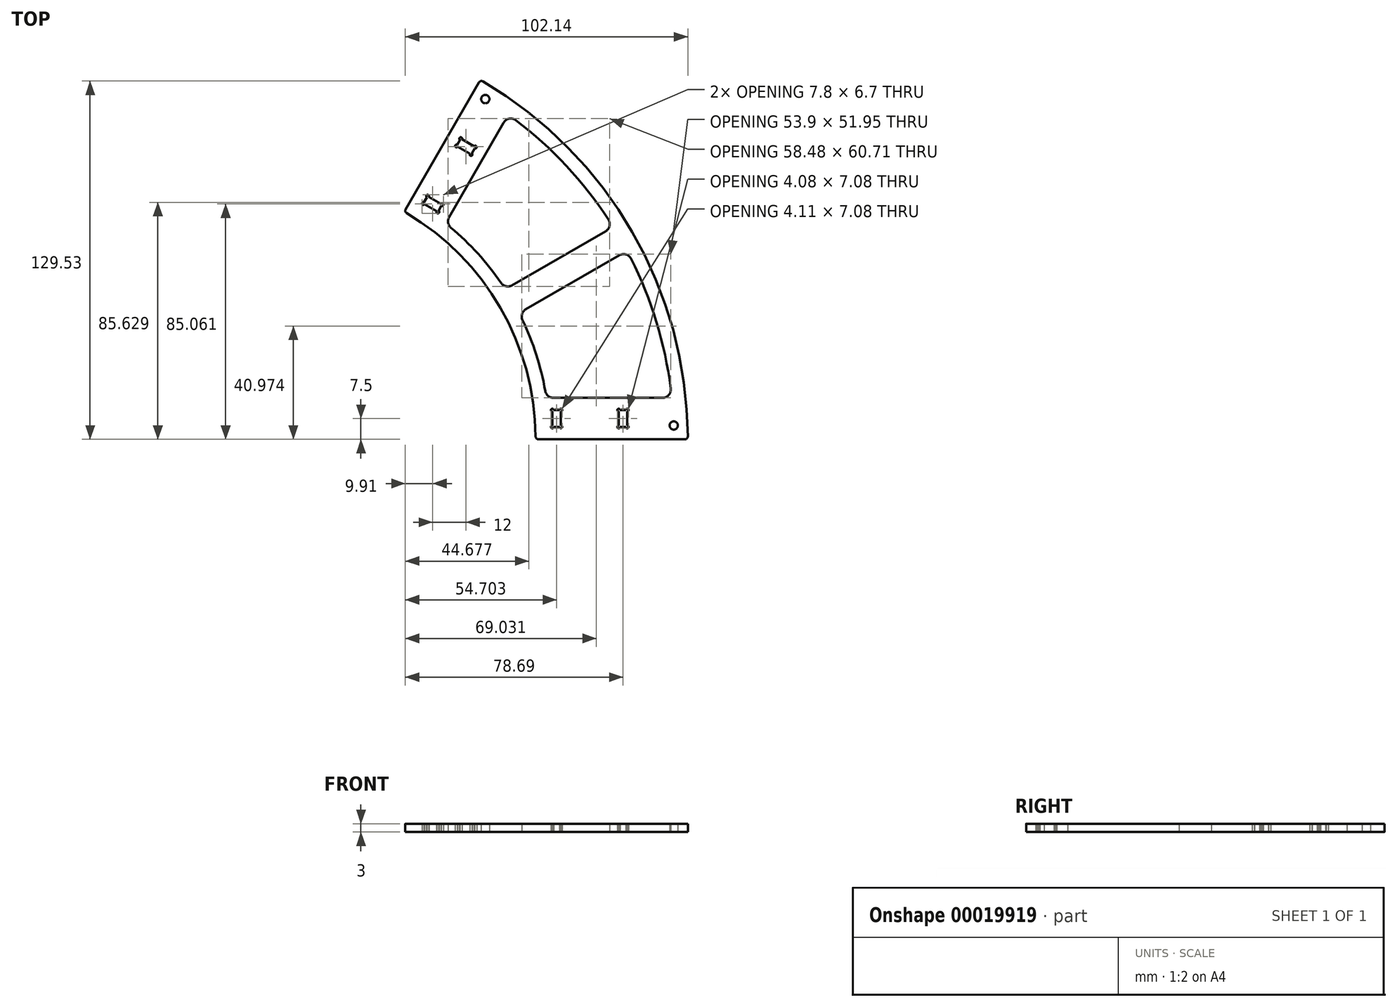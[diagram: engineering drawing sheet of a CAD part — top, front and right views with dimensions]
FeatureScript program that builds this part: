
annotation { "Feature Type Name" : "Feature", "Feature Type Description" : "" }
export const myFeature = defineFeature(function(context is Context, id is Id, definition is map)
    precondition{}
    {
        {
            var Q0;
            Q0=qCreatedBy(makeId("Top.planeOp"),FACE);
            var sketch = newSketch(context, id + "F1", { "sketchPlane" : qUnion([Q0])});
            skArc(sketch, "E0", {"start": v(150, 1) * mm, "mid": v(129.9, 75) * mm, "end": v(75.87, 129.4) * mm});
            skArc(sketch, "E1", {"start": v(95, 0.99) * mm, "mid": v(82.27, 47.5) * mm, "end": v(48.35, 81.77) * mm});
            skLineSegment(sketch, "E2", {"start": v(95, 0) * mm, "end": v(150, 0) * mm});
            skLineSegment(sketch, "E3", {"start": v(149, 0) * mm, "end": v(96, 0) * mm});
            skLineSegment(sketch, "E4", {"start": v(74.5, 129.03) * mm, "end": v(48, 83.13) * mm});
            skArc(sketch, "E5", {"start": v(143.83, 18.38) * mm, "mid": v(138.64, 42.46) * mm, "end": v(129.46, 65.31) * mm});
            skArc(sketch, "E6", {"start": v(98.46, 17.48) * mm, "mid": v(95.21, 30.58) * mm, "end": v(90.22, 43.12) * mm});
            skLineSegment(sketch, "E7", {"start": v(63.7, 80.33) * mm, "end": v(83.42, 114.48) * mm});
            skLineSegment(sketch, "E8", {"start": v(101.41, 15) * mm, "end": v(140.85, 15) * mm});
            skLineSegment(sketch, "E9", {"start": v(86.43, 55.67) * mm, "end": v(120.28, 75.22) * mm});
            skLineSegment(sketch, "E10", {"start": v(91.43, 47.01) * mm, "end": v(125.28, 66.56) * mm});
            skArc(sketch, "E11.trimOffspring", {"start": v(82.46, 56.58) * mm, "mid": v(74.09, 67.17) * mm, "end": v(64.37, 76.53) * mm});
            skArc(sketch, "E12.trimOffspring", {"start": v(121.29, 79.46) * mm, "mid": v(106.1, 98.84) * mm, "end": v(87.83, 115.37) * mm});
            skLineSegment(sketch, "E13", {"start": v(0, 0) * mm, "end": v(189.98, 109.68) * mm, "construction": true});
            skPoint(sketch, "E14.visualSharp", {"position": v(85.1, 117.4) * mm});
            skArc(sketch, "E14.filletArc", {"start": v(87.83, 115.37) * mm, "mid": v(85.42, 115.92) * mm, "end": v(83.42, 114.48) * mm});
            skPoint(sketch, "E15.visualSharp", {"position": v(123, 76.79) * mm});
            skArc(sketch, "E15.filletArc", {"start": v(120.28, 75.22) * mm, "mid": v(121.7, 77.12) * mm, "end": v(121.29, 79.46) * mm});
            skPoint(sketch, "E16.visualSharp", {"position": v(128, 68.13) * mm});
            skArc(sketch, "E16.filletArc", {"start": v(129.46, 65.31) * mm, "mid": v(127.64, 66.83) * mm, "end": v(125.28, 66.56) * mm});
            skPoint(sketch, "E17.visualSharp", {"position": v(144.22, 15) * mm});
            skArc(sketch, "E17.filletArc", {"start": v(140.85, 15) * mm, "mid": v(143.1, 16.02) * mm, "end": v(143.83, 18.38) * mm});
            skPoint(sketch, "E18.visualSharp", {"position": v(98.87, 15) * mm});
            skArc(sketch, "E18.filletArc", {"start": v(98.46, 17.48) * mm, "mid": v(99.49, 15.7) * mm, "end": v(101.41, 15) * mm});
            skPoint(sketch, "E19.visualSharp", {"position": v(89, 45.6) * mm});
            skArc(sketch, "E19.filletArc", {"start": v(91.43, 47.01) * mm, "mid": v(90.07, 45.3) * mm, "end": v(90.22, 43.12) * mm});
            skPoint(sketch, "E20.visualSharp", {"position": v(84, 54.27) * mm});
            skArc(sketch, "E20.filletArc", {"start": v(82.46, 56.58) * mm, "mid": v(84.27, 55.35) * mm, "end": v(86.43, 55.67) * mm});
            skPoint(sketch, "E21.visualSharp", {"position": v(62.42, 78.12) * mm});
            skArc(sketch, "E21.filletArc", {"start": v(63.7, 80.33) * mm, "mid": v(63.34, 78.3) * mm, "end": v(64.37, 76.53) * mm});
            skPoint(sketch, "E22.visualSharp", {"position": v(47.5, 82.27) * mm});
            skArc(sketch, "E22.filletArc", {"start": v(48, 83.13) * mm, "mid": v(47.9, 82.38) * mm, "end": v(48.35, 81.77) * mm});
            skPoint(sketch, "E23.visualSharp", {"position": v(75, 129.9) * mm});
            skArc(sketch, "E23.filletArc", {"start": v(75.87, 129.4) * mm, "mid": v(75.1, 129.5) * mm, "end": v(74.5, 129.03) * mm});
            skPoint(sketch, "E24.visualSharp", {"position": v(150, 0) * mm});
            skArc(sketch, "E24.filletArc", {"start": v(149, 0) * mm, "mid": v(149.7, 0.3) * mm, "end": v(150, 1) * mm});
            skPoint(sketch, "E25.visualSharp", {"position": v(95, 0) * mm});
            skArc(sketch, "E25.filletArc", {"start": v(95, 0.99) * mm, "mid": v(95.3, 0.29) * mm, "end": v(96, 0) * mm});
            skLineSegment(sketch, "E26", {"start": v(100, 4.62) * mm, "end": v(100, -10.43) * mm, "construction": true});
            skLineSegment(sketch, "E27.bottom", {"start": v(101.5, 10.55) * mm, "end": v(103.6, 10.55) * mm});
            skLineSegment(sketch, "E27.top", {"start": v(101.5, 4.45) * mm, "end": v(103.62, 4.45) * mm});
            skLineSegment(sketch, "E27.left", {"start": v(101, 10.05) * mm, "end": v(101, 4.95) * mm});
            skLineSegment(sketch, "E27.right", {"start": v(104.1, 10.05) * mm, "end": v(104.1, 5) * mm});
            skArc(sketch, "E28", {"start": v(101.5, 10.55) * mm, "mid": v(100.65, 10.9) * mm, "end": v(101, 10.05) * mm});
            skArc(sketch, "E29", {"start": v(103.62, 4.45) * mm, "mid": v(104.5, 4.18) * mm, "end": v(104.1, 5) * mm});
            skArc(sketch, "E30", {"start": v(101, 4.95) * mm, "mid": v(100.65, 4.1) * mm, "end": v(101.5, 4.45) * mm});
            skArc(sketch, "E31", {"start": v(104.1, 10.05) * mm, "mid": v(104.45, 10.9) * mm, "end": v(103.6, 10.55) * mm});
            skLineSegment(sketch, "E32", {"start": v(36.09, 94.63) * mm, "end": v(64.73, 78.1) * mm, "construction": true});
            skLineSegment(sketch, "E33", {"start": v(54.79, 85) * mm, "end": v(59.2, 82.44) * mm});
            skLineSegment(sketch, "E34", {"start": v(59.89, 82.63) * mm, "end": v(60.94, 84.45) * mm});
            skLineSegment(sketch, "E35", {"start": v(60.75, 85.13) * mm, "end": v(56.34, 87.68) * mm});
            skLineSegment(sketch, "E36", {"start": v(54.6, 85.68) * mm, "end": v(55.65, 87.5) * mm});
            skArc(sketch, "E37", {"start": v(56.34, 87.68) * mm, "mid": v(55.77, 88.41) * mm, "end": v(55.65, 87.5) * mm});
            skArc(sketch, "E38", {"start": v(60.94, 84.45) * mm, "mid": v(61.67, 85) * mm, "end": v(60.75, 85.13) * mm});
            skArc(sketch, "E39", {"start": v(54.6, 85.68) * mm, "mid": v(53.87, 85.11) * mm, "end": v(54.79, 85) * mm});
            skArc(sketch, "E40", {"start": v(59.2, 82.44) * mm, "mid": v(59.77, 81.71) * mm, "end": v(59.89, 82.63) * mm});
            skCircle(sketch, "E41", {"center": v(144.91, 5) * mm, "radius": 1.5 * mm});
            skCircle(sketch, "E42", {"center": v(76.79, 123) * mm, "radius": 1.5 * mm});
            skLineSegment(sketch, "E43.bottom", {"start": v(125.5, 10.55) * mm, "end": v(127.6, 10.55) * mm});
            skLineSegment(sketch, "E43.top", {"start": v(125.5, 4.45) * mm, "end": v(127.6, 4.45) * mm});
            skLineSegment(sketch, "E43.left", {"start": v(125, 10.05) * mm, "end": v(125, 4.95) * mm});
            skLineSegment(sketch, "E43.right", {"start": v(128.1, 10.05) * mm, "end": v(128.1, 4.95) * mm});
            skArc(sketch, "E44", {"start": v(125.5, 10.55) * mm, "mid": v(124.65, 10.9) * mm, "end": v(125, 10.05) * mm});
            skArc(sketch, "E45", {"start": v(128.1, 10.05) * mm, "mid": v(128.45, 10.9) * mm, "end": v(127.6, 10.55) * mm});
            skArc(sketch, "E46", {"start": v(127.6, 4.45) * mm, "mid": v(128.45, 4.1) * mm, "end": v(128.1, 4.95) * mm});
            skArc(sketch, "E47", {"start": v(125, 4.95) * mm, "mid": v(124.65, 4.1) * mm, "end": v(125.5, 4.45) * mm});
            skLineSegment(sketch, "E48", {"start": v(66.79, 105.78) * mm, "end": v(71.2, 103.23) * mm});
            skLineSegment(sketch, "E49", {"start": v(71.89, 103.41) * mm, "end": v(72.94, 105.23) * mm});
            skLineSegment(sketch, "E50", {"start": v(72.75, 105.91) * mm, "end": v(68.34, 108.46) * mm});
            skLineSegment(sketch, "E51", {"start": v(67.65, 108.28) * mm, "end": v(66.6, 106.46) * mm});
            skArc(sketch, "E52", {"start": v(68.34, 108.46) * mm, "mid": v(67.77, 109.2) * mm, "end": v(67.65, 108.28) * mm});
            skArc(sketch, "E53", {"start": v(72.94, 105.23) * mm, "mid": v(73.67, 105.8) * mm, "end": v(72.75, 105.91) * mm});
            skArc(sketch, "E54", {"start": v(71.2, 103.23) * mm, "mid": v(71.77, 102.5) * mm, "end": v(71.89, 103.41) * mm});
            skArc(sketch, "E55", {"start": v(66.6, 106.46) * mm, "mid": v(65.87, 105.9) * mm, "end": v(66.79, 105.78) * mm});
            skSolve(sketch);
        }
        {
            var Q0;
            Q0 = qSketchRegion(id + "F1", true);
            extrude(context, id + "F0", {"entities" : qUnion([Q0]), "depth" : 3 * mm});
        }
    });
